# Revit family: 820-00-024 DN450-1000
name_source: partatom
category: Pipe Accessories
units: mm (PartAtom-declared; Revit-internal decimal feet)

## family parameters
Always vertical = Yes
Cut with Voids When Loaded = No
Part Type = Valve - Breaks Into
Round Connector Dimension = Use Diameter
Shared = No
Work Plane-Based = No

## types (14) — shared parameters
1 = 1 mm  [stored 0.00328084 ft]
90 = 90 mm
Body_wallthickness = 10 mm  [stored 0.0328084 ft]
DN1000_PN10 = 820-1000-00-02060031002
DN1000_PN16 = 820-1000-00-02060161002
DN450_PN10 = 820-0450-00-02060031002
DN450_PN16 = 820-0450-00-02060161002
DN500_PN10 = 820-0500-00-02060031002
DN500_PN16 = 820-0500-00-02060161002
DN600_PN10 = 820-0600-00-02060031002
DN600_PN16 = 820-0600-00-02060161002
DN700_PN10 = 820-0700-00-02060031002
DN700_PN16 = 820-0700-00-02060161002
DN800_PN10 = 820-0800-00-02060031002
DN800_PN16 = 820-0800-00-02060161002
DN900_PN10 = 820-0900-00-02060031002
DN900_PN16 = 820-0900-00-02060161002
Description_ = AVK CENTRIC BUTTERFLY VALVE WAFER TYPE, PN10/16
FL_T = 15 mm  [stored 0.0492126 ft]
Search_table = 820-00-024 DN450-1000
URL product pages = https://www.avkvalves.com
fillet = 20 mm  [stored 0.0656168 ft]
fillte1 = 10 mm  [stored 0.0328084 ft]
zero-valued in all types: Default Elevation

## per-type parameters (varying)
- DN1000_PN10: Actuator_Dia=350 mm; Bore=500 mm; DN=1000 mm; EPDM=499 mm; EPDM_R=510 mm; F=80 mm  [stored 0.262467 ft]; F2=100 mm; FL_R=510 mm; Fillet=50 mm  [stored 0.164042 ft]; Flange_thickness=15 mm  [stored 0.0492126 ft]; H2=693 mm; Hole_L=175 mm; Hole_L1=587 mm; Hole_dia=50 mm  [stored 0.164042 ft]; ID=500 mm; L=218 mm; L-2=216 mm; L2=567 mm; LUG_T=108 mm; L_ref=186 mm; L_ref_2=372 mm; L_ref_3=155 mm; Lug_D=35 mm  [stored 0.114829 ft]; PCD=580 mm; W2_ref=745 mm; Wafer_Dim2=653 mm; Wafer_dim=227 mm; Wafer_dim1=680 mm; Width_dim=280 mm; disk=81 mm  [stored 0.265748 ft]
- DN1000_PN16: Actuator_Dia=350 mm; Bore=500 mm; DN=1000 mm; EPDM=499 mm; EPDM_R=510 mm; F=80 mm  [stored 0.262467 ft]; F2=100 mm; FL_R=510 mm; Fillet=50 mm  [stored 0.164042 ft]; Flange_thickness=15 mm  [stored 0.0492126 ft]; H2=693 mm; Hole_L=175 mm; Hole_L1=587 mm; Hole_dia=50 mm  [stored 0.164042 ft]; ID=500 mm; L=218 mm; L-2=216 mm; L2=567 mm; LUG_T=108 mm; L_ref=186 mm; L_ref_2=372 mm; L_ref_3=155 mm; Lug_D=35 mm  [stored 0.114829 ft]; PCD=585 mm; W2_ref=745 mm; Wafer_Dim2=653 mm; Wafer_dim=227 mm; Wafer_dim1=680 mm; Width_dim=280 mm; disk=81 mm  [stored 0.265748 ft]
- DN450_PN10: Actuator_Dia=175 mm; Bore=225 mm; DN=450 mm; EPDM=224 mm; EPDM_R=242 mm; F=45 mm  [stored 0.147638 ft]; F2=65 mm  [stored 0.213255 ft]; FL_R=235 mm; Fillet=30 mm  [stored 0.0984252 ft]; Flange_thickness=11 mm  [stored 0.0360892 ft]; H2=355 mm; Hole_L=88 mm; Hole_L1=279 mm; Hole_dia=30 mm  [stored 0.0984252 ft]; ID=225 mm; L=113 mm; L-2=111 mm; L2=269 mm; LUG_T=56 mm  [stored 0.183727 ft]; L_ref=89 mm  [stored 0.291995 ft]; L_ref_2=178 mm; L_ref_3=74 mm; Lug_D=21 mm  [stored 0.0688976 ft]; PCD=283 mm; W2_ref=397 mm; Wafer_Dim2=310 mm; Wafer_dim=108 mm; Wafer_dim1=323 mm; Width_dim=149 mm; disk=42 mm
- DN450_PN16: Actuator_Dia=175 mm; Bore=225 mm; DN=450 mm; EPDM=224 mm; EPDM_R=242 mm; F=45 mm  [stored 0.147638 ft]; F2=65 mm  [stored 0.213255 ft]; FL_R=235 mm; Fillet=30 mm  [stored 0.0984252 ft]; Flange_thickness=12 mm  [stored 0.0393701 ft]; H2=355 mm; Hole_L=88 mm; Hole_L1=279 mm; Hole_dia=30 mm  [stored 0.0984252 ft]; ID=225 mm; L=113 mm; L-2=111 mm; L2=269 mm; LUG_T=56 mm  [stored 0.183727 ft]; L_ref=87 mm  [stored 0.285433 ft]; L_ref_2=174 mm; L_ref_3=73 mm; Lug_D=21 mm  [stored 0.0688976 ft]; PCD=293 mm; W2_ref=397 mm; Wafer_Dim2=310 mm; Wafer_dim=108 mm; Wafer_dim1=323 mm; Width_dim=149 mm; disk=42 mm
- DN500_PN10: Actuator_Dia=175 mm; Bore=250 mm; DN=500 mm; EPDM=249 mm; EPDM_R=268 mm; F=45 mm  [stored 0.147638 ft]; F2=65 mm  [stored 0.213255 ft]; FL_R=260 mm; Fillet=32 mm  [stored 0.104987 ft]; Flange_thickness=12 mm  [stored 0.0393701 ft]; H2=393 mm; Hole_L=88 mm; Hole_L1=308 mm; Hole_dia=32 mm  [stored 0.104987 ft]; ID=250 mm; L=126 mm; L-2=124 mm; L2=298 mm; LUG_T=62 mm  [stored 0.203412 ft]; L_ref=100 mm; L_ref_2=200 mm; L_ref_3=83 mm  [stored 0.27231 ft]; Lug_D=22 mm; PCD=310 mm; W2_ref=437 mm; Wafer_Dim2=343 mm; Wafer_dim=119 mm; Wafer_dim1=357 mm; Width_dim=149 mm; disk=47 mm
- DN500_PN16: Actuator_Dia=175 mm; Bore=250 mm; DN=500 mm; EPDM=249 mm; EPDM_R=268 mm; F=45 mm  [stored 0.147638 ft]; F2=65 mm  [stored 0.213255 ft]; FL_R=260 mm; Fillet=32 mm  [stored 0.104987 ft]; Flange_thickness=13 mm  [stored 0.0426509 ft]; H2=393 mm; Hole_L=88 mm; Hole_L1=308 mm; Hole_dia=32 mm  [stored 0.104987 ft]; ID=250 mm; L=126 mm; L-2=124 mm; L2=298 mm; LUG_T=62 mm  [stored 0.203412 ft]; L_ref=98 mm; L_ref_2=196 mm; L_ref_3=82 mm  [stored 0.269029 ft]; Lug_D=22 mm; PCD=325 mm; W2_ref=437 mm; Wafer_Dim2=343 mm; Wafer_dim=119 mm; Wafer_dim1=357 mm; Width_dim=149 mm; disk=47 mm
- DN600_PN10: Actuator_Dia=210 mm; Bore=300 mm; DN=600 mm; EPDM=299 mm; EPDM_R=313 mm; F=70 mm  [stored 0.229659 ft]; F2=80 mm  [stored 0.262467 ft]; FL_R=310 mm; Fillet=36 mm  [stored 0.11811 ft]; Flange_thickness=13 mm  [stored 0.0426509 ft]; H2=464 mm; Hole_L=105 mm; Hole_L1=360 mm; Hole_dia=36 mm  [stored 0.11811 ft]; ID=300 mm; L=153 mm; L-2=151 mm; L2=348 mm; LUG_T=76 mm; L_ref=125 mm; L_ref_2=250 mm; L_ref_3=104 mm; Lug_D=25 mm  [stored 0.082021 ft]; PCD=363 mm; W2_ref=522 mm; Wafer_Dim2=400 mm; Wafer_dim=139 mm; Wafer_dim1=417 mm; Width_dim=179 mm; disk=57 mm
- DN600_PN16: Actuator_Dia=210 mm; Bore=300 mm; DN=600 mm; EPDM=299 mm; EPDM_R=313 mm; F=70 mm  [stored 0.229659 ft]; F2=80 mm  [stored 0.262467 ft]; FL_R=310 mm; Fillet=36 mm  [stored 0.11811 ft]; Flange_thickness=14 mm  [stored 0.0459318 ft]; H2=464 mm; Hole_L=105 mm; Hole_L1=360 mm; Hole_dia=36 mm  [stored 0.11811 ft]; ID=300 mm; L=153 mm; L-2=151 mm; L2=348 mm; LUG_T=76 mm; L_ref=123 mm; L_ref_2=246 mm; L_ref_3=103 mm; Lug_D=25 mm  [stored 0.082021 ft]; PCD=385 mm; W2_ref=522 mm; Wafer_Dim2=400 mm; Wafer_dim=139 mm; Wafer_dim1=417 mm; Width_dim=179 mm; disk=57 mm
- DN700_PN10: Actuator_Dia=300 mm; Bore=350 mm; DN=700 mm; EPDM=349 mm; EPDM_R=360 mm; F=70 mm  [stored 0.229659 ft]; F2=80 mm  [stored 0.262467 ft]; FL_R=360 mm; Fillet=40 mm  [stored 0.131234 ft]; Flange_thickness=14 mm  [stored 0.0459318 ft]; H2=503 mm; Hole_L=150 mm; Hole_L1=415 mm; Hole_dia=40 mm  [stored 0.131234 ft]; ID=350 mm; L=168 mm; L-2=166 mm; L2=400 mm; LUG_T=83 mm  [stored 0.27231 ft]; L_ref=138 mm; L_ref_2=276 mm; L_ref_3=115 mm; Lug_D=28 mm  [stored 0.0918635 ft]; PCD=420 mm; W2_ref=565 mm; Wafer_Dim2=461 mm; Wafer_dim=160 mm; Wafer_dim1=480 mm; Width_dim=210 mm; disk=62 mm  [stored 0.203412 ft]
- DN700_PN16: Actuator_Dia=300 mm; Bore=350 mm; DN=700 mm; EPDM=349 mm; EPDM_R=360 mm; F=70 mm  [stored 0.229659 ft]; F2=80 mm  [stored 0.262467 ft]; FL_R=360 mm; Fillet=40 mm  [stored 0.131234 ft]; Flange_thickness=14 mm  [stored 0.0459318 ft]; H2=503 mm; Hole_L=150 mm; Hole_L1=415 mm; Hole_dia=40 mm  [stored 0.131234 ft]; ID=350 mm; L=168 mm; L-2=166 mm; L2=400 mm; LUG_T=83 mm  [stored 0.27231 ft]; L_ref=138 mm; L_ref_2=276 mm; L_ref_3=115 mm; Lug_D=28 mm  [stored 0.0918635 ft]; PCD=420 mm; W2_ref=565 mm; Wafer_Dim2=461 mm; Wafer_dim=160 mm; Wafer_dim1=480 mm; Width_dim=210 mm; disk=62 mm  [stored 0.203412 ft]
- DN800_PN10: Actuator_Dia=300 mm; Bore=400 mm; DN=800 mm; EPDM=399 mm; EPDM_R=409 mm; F=70 mm  [stored 0.229659 ft]; F2=80 mm  [stored 0.262467 ft]; FL_R=410 mm; Fillet=43 mm  [stored 0.141076 ft]; Flange_thickness=14 mm  [stored 0.0459318 ft]; H2=577 mm; Hole_L=150 mm; Hole_L1=471 mm; Hole_dia=43 mm  [stored 0.141076 ft]; ID=400 mm; L=190 mm; L-2=188 mm; L2=454 mm; LUG_T=94 mm; L_ref=160 mm; L_ref_2=320 mm; L_ref_3=133 mm; Lug_D=30 mm  [stored 0.0984252 ft]; PCD=475 mm; W2_ref=627 mm; Wafer_Dim2=523 mm; Wafer_dim=182 mm; Wafer_dim1=545 mm; Width_dim=235 mm; disk=71 mm
- DN800_PN16: Actuator_Dia=300 mm; Bore=400 mm; DN=800 mm; EPDM=399 mm; EPDM_R=409 mm; F=70 mm  [stored 0.229659 ft]; F2=80 mm  [stored 0.262467 ft]; FL_R=410 mm; Fillet=43 mm  [stored 0.141076 ft]; Flange_thickness=14 mm  [stored 0.0459318 ft]; H2=577 mm; Hole_L=150 mm; Hole_L1=471 mm; Hole_dia=43 mm  [stored 0.141076 ft]; ID=400 mm; L=190 mm; L-2=188 mm; L2=454 mm; LUG_T=94 mm; L_ref=160 mm; L_ref_2=320 mm; L_ref_3=133 mm; Lug_D=30 mm  [stored 0.0984252 ft]; PCD=475 mm; W2_ref=627 mm; Wafer_Dim2=523 mm; Wafer_dim=182 mm; Wafer_dim1=545 mm; Width_dim=235 mm; disk=71 mm
- DN900_PN10: Actuator_Dia=350 mm; Bore=450 mm; DN=900 mm; EPDM=449 mm; EPDM_R=457 mm; F=80 mm  [stored 0.262467 ft]; F2=100 mm; FL_R=460 mm; Fillet=46 mm  [stored 0.150919 ft]; Flange_thickness=15 mm  [stored 0.0492126 ft]; H2=643 mm; Hole_L=175 mm; Hole_L1=526 mm; Hole_dia=46 mm  [stored 0.150919 ft]; ID=450 mm; L=204 mm; L-2=202 mm; L2=508 mm; LUG_T=101 mm; L_ref=172 mm; L_ref_2=344 mm; L_ref_3=143 mm; Lug_D=32 mm  [stored 0.104987 ft]; PCD=525 mm; W2_ref=696 mm; Wafer_Dim2=585 mm; Wafer_dim=203 mm; Wafer_dim1=609 mm; Width_dim=275 mm; disk=76 mm
- DN900_PN16: Actuator_Dia=350 mm; Bore=450 mm; DN=900 mm; EPDM=449 mm; EPDM_R=457 mm; F=80 mm  [stored 0.262467 ft]; F2=100 mm; FL_R=460 mm; Fillet=46 mm  [stored 0.150919 ft]; Flange_thickness=15 mm  [stored 0.0492126 ft]; H2=643 mm; Hole_L=175 mm; Hole_L1=526 mm; Hole_dia=46 mm  [stored 0.150919 ft]; ID=450 mm; L=204 mm; L-2=202 mm; L2=508 mm; LUG_T=101 mm; L_ref=172 mm; L_ref_2=344 mm; L_ref_3=143 mm; Lug_D=32 mm  [stored 0.104987 ft]; PCD=525 mm; W2_ref=696 mm; Wafer_Dim2=585 mm; Wafer_dim=203 mm; Wafer_dim1=609 mm; Width_dim=275 mm; disk=76 mm

note: [stored X ft] marks values corroborated as IEEE doubles in the binary element streams (Revit-internal decimal feet)

## geometry (parser evidence)
native form markers: Sweep x5
no freeform markers — native parametric forms only
